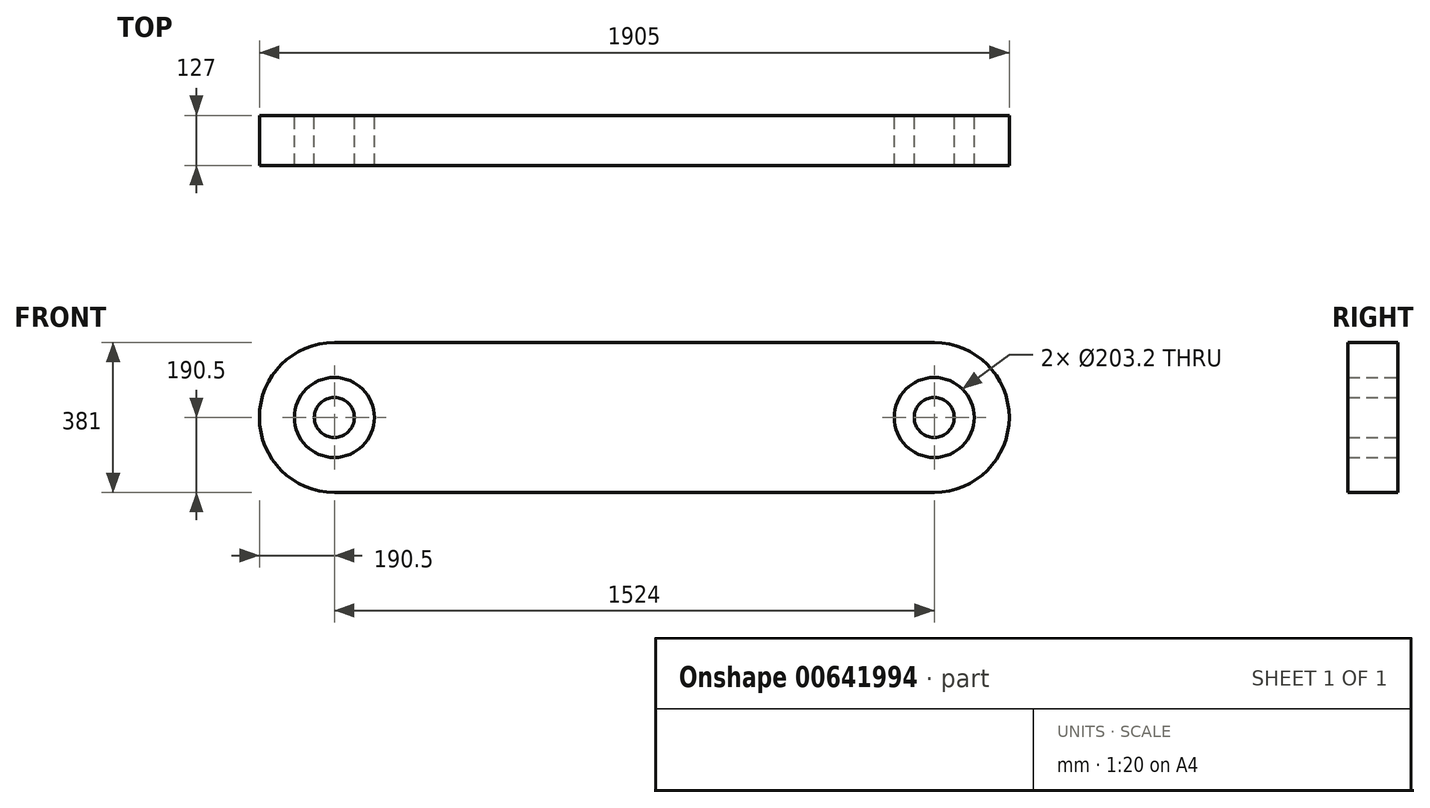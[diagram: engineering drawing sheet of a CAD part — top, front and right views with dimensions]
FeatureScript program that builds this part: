
annotation { "Feature Type Name" : "Feature", "Feature Type Description" : "" }
export const myFeature = defineFeature(function(context is Context, id is Id, definition is map)
    precondition{}
    {
        {
            var Q0;
            Q0=qCreatedBy(makeId("Front.planeOp"),FACE);
            var sketch = newSketch(context, id + "F0", { "sketchPlane" : qUnion([Q0])});
            skArc(sketch, "E0", {"start": v(0, 190.5) * mm, "mid": v(-190.5, 0) * mm, "end": v(0, -190.5) * mm});
            skArc(sketch, "E1", {"start": v(1524, -190.5) * mm, "mid": v(1714.5, 0) * mm, "end": v(1524, 190.5) * mm});
            skLineSegment(sketch, "E2", {"start": v(0, 190.5) * mm, "end": v(1524, 190.5) * mm});
            skLineSegment(sketch, "E3", {"start": v(0, -190.5) * mm, "end": v(1524, -190.5) * mm});
            skCircle(sketch, "E4", {"center": v(0, 0) * mm, "radius": 101.6 * mm});
            skCircle(sketch, "E5", {"center": v(1524, 0) * mm, "radius": 101.6 * mm});
            skCircle(sketch, "E6", {"center": v(0, 0) * mm, "radius": 50.8 * mm});
            skCircle(sketch, "E7", {"center": v(1524, 0) * mm, "radius": 50.8 * mm});
            skSolve(sketch);
        }
        {
            var Q0;
            Q0=makeQuery(id+"F0.imprint","IMPRINT",FACE,{"disambiguationData":[TD([[makeQuery(id+"F0.imprint","IMPRINT",EDGE,{"derivedFrom":sQuery(id+"F0.wireOp",EDGE,"E6")}),1.0]])]});
            var Q1;
            Q1=makeQuery(id+"F0.imprint","IMPRINT",FACE,{"disambiguationData":[TD([[makeQuery(id+"F0.imprint","IMPRINT",EDGE,{"derivedFrom":sQuery(id+"F0.wireOp",EDGE,"E0")}),1.0]])]});
            var Q2;
            Q2=makeQuery(id+"F0.imprint","IMPRINT",FACE,{"disambiguationData":[TD([[makeQuery(id+"F0.imprint","IMPRINT",EDGE,{"derivedFrom":sQuery(id+"F0.wireOp",EDGE,"E7")}),1.0]])]});
            extrude(context, id + "F1", {"entities" : qUnion([Q0, Q1, Q2]), "depth" : 127 * mm, "offsetDistance" : 25.4 * mm});
        }
    });
